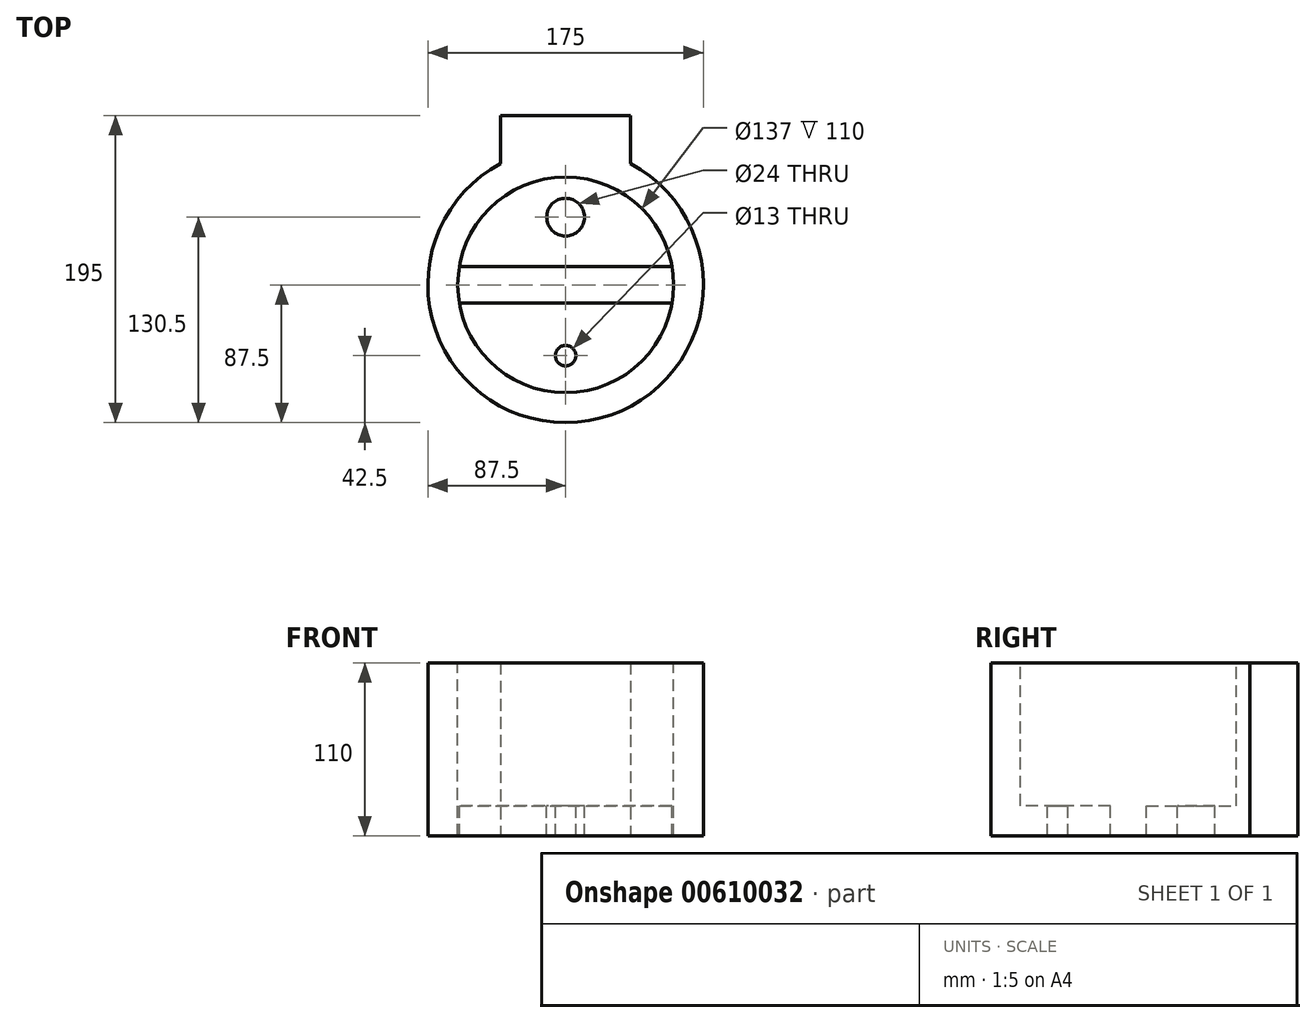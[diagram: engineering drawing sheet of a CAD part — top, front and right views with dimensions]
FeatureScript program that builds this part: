
annotation { "Feature Type Name" : "Feature", "Feature Type Description" : "" }
export const myFeature = defineFeature(function(context is Context, id is Id, definition is map)
    precondition{}
    {
        {
            var Q0;
            Q0=qCreatedBy(makeId("Top.planeOp"),FACE);
            var sketch = newSketch(context, id + "F0", { "sketchPlane" : qUnion([Q0])});
            skLineSegment(sketch, "E0.bottom", {"start": v(165, -150) * mm, "end": v(-165, -150) * mm});
            skLineSegment(sketch, "E0.top", {"start": v(165, 150) * mm, "end": v(-165, 150) * mm});
            skLineSegment(sketch, "E0.left", {"start": v(165, -150) * mm, "end": v(165, 150) * mm});
            skLineSegment(sketch, "E0.right", {"start": v(-165, -150) * mm, "end": v(-165, 150) * mm});
            skPoint(sketch, "E0.middle", {"position": v(0, 0) * mm});
            skSolve(sketch);
        }
        {
            var Q0;
            Q0=makeQuery(id+"F0.imprint","IMPRINT",FACE,{"disambiguationData":[TD([[makeQuery(id+"F0.imprint","IMPRINT",EDGE,{"derivedFrom":sQuery(id+"F0.wireOp",EDGE,"E0.bottom")}),-1.0]])]});
            extrude(context, id + "F1", {"entities" : qUnion([Q0]), "oppositeDirection" : true, "depth" : 110 * mm, "offsetDistance" : 25 * mm});
        }
        {
            var Q0;
            Q0=qCreatedBy(makeId("Top.planeOp"),FACE);
            var sketch = newSketch(context, id + "F2", { "sketchPlane" : qUnion([Q0])});
            skCircle(sketch, "E1", {"center": v(0, 0) * mm, "radius": 68.5 * mm});
            skCircle(sketch, "E2", {"center": v(0, 0) * mm, "radius": 87.5 * mm});
            skLineSegment(sketch, "E3.bottom", {"start": v(165, -150) * mm, "end": v(-165, -150) * mm});
            skLineSegment(sketch, "E3.top", {"start": v(165, 150) * mm, "end": v(-165, 150) * mm});
            skLineSegment(sketch, "E3.left", {"start": v(165, -150) * mm, "end": v(165, 150) * mm});
            skLineSegment(sketch, "E3.right", {"start": v(-165, -150) * mm, "end": v(-165, 150) * mm});
            skSolve(sketch);
        }
        {
            var Q0;
            Q0=makeQuery(id+"F2.imprint","IMPRINT",FACE,{"disambiguationData":[TD([[makeQuery(id+"F2.imprint","IMPRINT",EDGE,{"derivedFrom":sQuery(id+"F2.wireOp",EDGE,"E1")}),1.0]])]});
            var Q1;
            Q1=sQuery(id+"F2.wireOp",EDGE,"E1");
            extrude(context, id + "F3", {"entities" : qUnion([Q0]), "operationType" : NewBodyOperationType.REMOVE, "surfaceEntities" : qUnion([Q1]), "oppositeDirection" : true, "depth" : 90.8 * mm, "offsetDistance" : 25 * mm});
        }
        {
            var Q0;
            Q0=makeQuery(id+"F3.boolean.opBoolean","COPY",FACE,{"derivedFrom":makeQuery(id+"F3.opExtrude","CAP_FACE",FACE,{"disambiguationData":[OSD([sQuery(id+"F2.wireOp",EDGE,"E1")])],"isStart":false})});
            var sketch = newSketch(context, id + "F4", { "sketchPlane" : qUnion([Q0])});
            skLineSegment(sketch, "E4", {"start": v(0, 0) * mm, "end": v(0, 43) * mm});
            skCircle(sketch, "E5", {"center": v(0, 43) * mm, "radius": 12 * mm});
            skLineSegment(sketch, "E6", {"start": v(0, 0) * mm, "end": v(0, -45) * mm});
            skCircle(sketch, "E7", {"center": v(0, -45) * mm, "radius": 6.5 * mm});
            skLineSegment(sketch, "E8.bottom", {"start": v(120, -11.5) * mm, "end": v(-120, -11.5) * mm});
            skLineSegment(sketch, "E8.top", {"start": v(120, 11.5) * mm, "end": v(-120, 11.5) * mm});
            skLineSegment(sketch, "E8.left", {"start": v(120, -11.5) * mm, "end": v(120, 11.5) * mm});
            skLineSegment(sketch, "E8.right", {"start": v(-120, -11.5) * mm, "end": v(-120, 11.5) * mm});
            skPoint(sketch, "E8.middle", {"position": v(0, 0) * mm});
            skSolve(sketch);
        }
        {
            var Q0;
            {var subQ1=sQuery(id+"F4.wireOp",EDGE,"E6");var subQ7=sQuery(id+"F4.wireOp",EDGE,"E4");var subQ8=makeQuery(id+"F4.imprint","INTERSECT",VERTEX,{"derivedFrom":[subQ7,subQ1]});Q0=makeQuery(id+"F4.imprint","IMPRINT",FACE,{"disambiguationData":[TD([[makeQuery(id+"F4.imprint","IMPRINT",EDGE,{"disambiguationData":[TD([[subQ8,-1.0]])],"derivedFrom":subQ7}),1.0]])]});}
            var Q1;
            {var subQ1=sQuery(id+"F4.wireOp",EDGE,"E4");var subQ5=sQuery(id+"F4.wireOp",EDGE,"E6");var subQ6=makeQuery(id+"F4.imprint","INTERSECT",VERTEX,{"derivedFrom":[subQ1,subQ5]});Q1=makeQuery(id+"F4.imprint","IMPRINT",FACE,{"disambiguationData":[TD([[makeQuery(id+"F4.imprint","IMPRINT",EDGE,{"disambiguationData":[TD([[subQ6,-1.0]])],"derivedFrom":subQ1}),-1.0]])]});}
            var Q2;
            Q2=makeQuery(id+"F4.imprint","IMPRINT",FACE,{"disambiguationData":[TD([[makeQuery(id+"F4.imprint","IMPRINT",EDGE,{"derivedFrom":sQuery(id+"F4.wireOp",EDGE,"E5")}),1.0]])]});
            var Q3;
            Q3=makeQuery(id+"F4.imprint","IMPRINT",FACE,{"disambiguationData":[TD([[makeQuery(id+"F4.imprint","IMPRINT",EDGE,{"derivedFrom":sQuery(id+"F4.wireOp",EDGE,"E7")}),1.0]])]});
            extrude(context, id + "F5", {"entities" : qUnion([Q0, Q1, Q2, Q3]), "operationType" : NewBodyOperationType.REMOVE, "endBound" : BoundingType.THROUGH_ALL, "oppositeDirection" : true, "depth" : 217 * mm, "offsetDistance" : 25 * mm});
        }
        {
            var Q0;
            Q0=makeQuery(id+"F2.imprint","IMPRINT",FACE,{"disambiguationData":[TD([[makeQuery(id+"F2.imprint","IMPRINT",EDGE,{"derivedFrom":sQuery(id+"F2.wireOp",EDGE,"E2")}),-1.0]])]});
            extrude(context, id + "F6", {"entities" : qUnion([Q0]), "operationType" : NewBodyOperationType.REMOVE, "endBound" : BoundingType.THROUGH_ALL, "oppositeDirection" : true, "depth" : 236 * mm, "offsetDistance" : 25 * mm});
        }
        {
            var Q0;
            Q0=makeQuery(id+"F1.opExtrude","CAP_FACE",FACE,{"disambiguationData":[OSD([sQuery(id+"F0.wireOp",EDGE,"E0.bottom"),sQuery(id+"F0.wireOp",EDGE,"E0.top"),sQuery(id+"F0.wireOp",EDGE,"E0.left"),sQuery(id+"F0.wireOp",EDGE,"E0.right")])],"isStart":false});
            var sketch = newSketch(context, id + "F7", { "sketchPlane" : qUnion([Q0])});
            skLineSegment(sketch, "E9.bottom", {"start": v(-41.25, -67.5) * mm, "end": v(41.25, -67.5) * mm});
            skLineSegment(sketch, "E9.top", {"start": v(-41.25, -107.5) * mm, "end": v(41.25, -107.5) * mm});
            skLineSegment(sketch, "E9.left", {"start": v(-41.25, -67.5) * mm, "end": v(-41.25, -107.5) * mm});
            skLineSegment(sketch, "E9.right", {"start": v(41.25, -67.5) * mm, "end": v(41.25, -107.5) * mm});
            skPoint(sketch, "E9.middle", {"position": v(0, -87.5) * mm});
            skSolve(sketch);
        }
        {
            var Q0;
            {var subQ0=sQuery(id+"F7.wireOp",EDGE,"E9.top");Q0=makeQuery(id+"F7.imprint","IMPRINT",FACE,{"disambiguationData":[TD([[makeQuery(id+"F7.imprint","IMPRINT",EDGE,{"derivedFrom":subQ0}),1.0]])]});}
            extrude(context, id + "F8", {"entities" : qUnion([Q0]), "operationType" : NewBodyOperationType.ADD, "oppositeDirection" : true, "depth" : 110 * mm, "offsetDistance" : 25 * mm});
        }
    });
